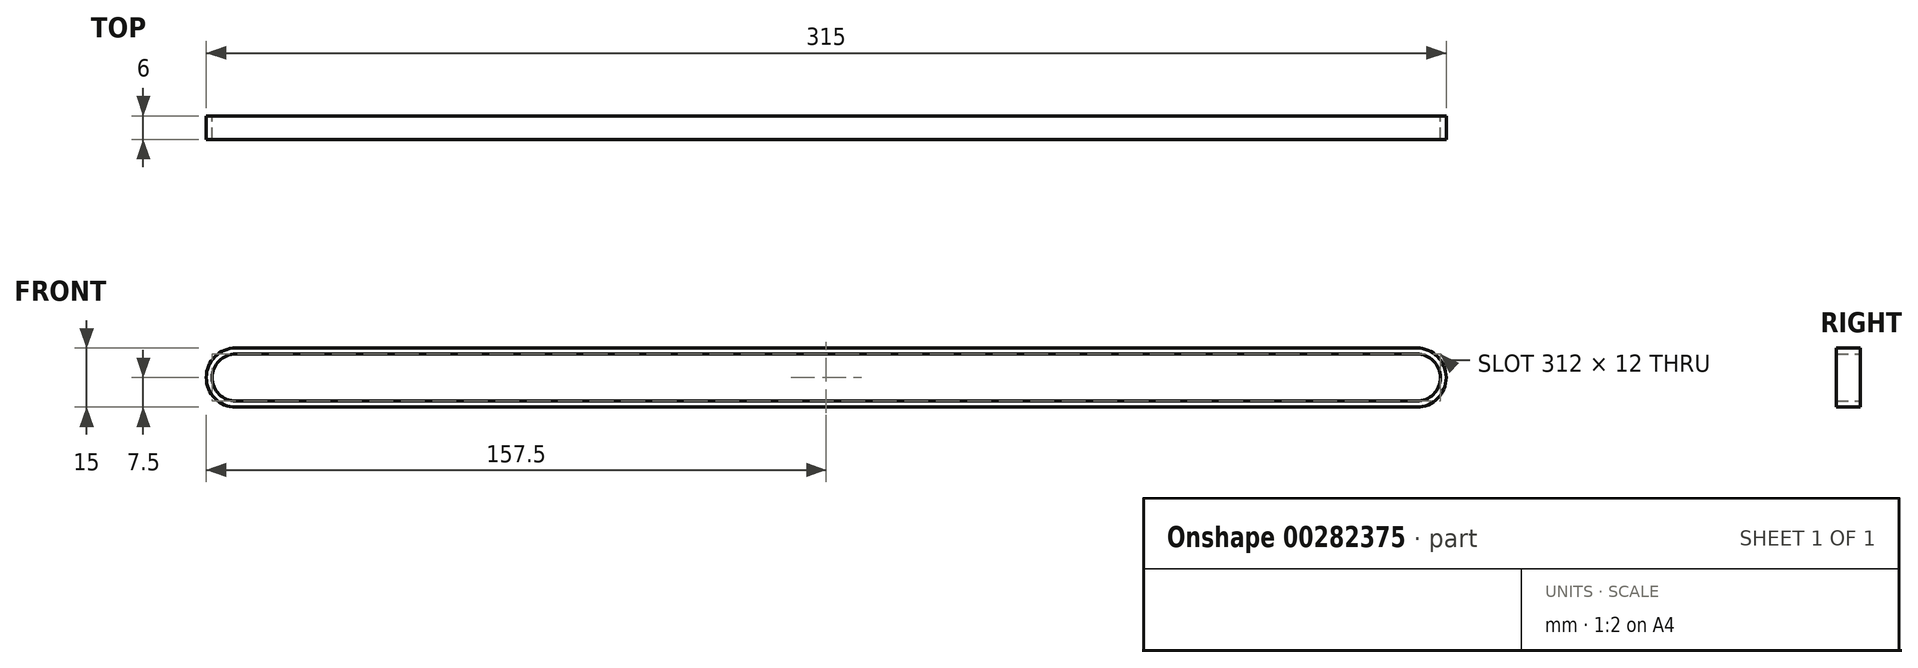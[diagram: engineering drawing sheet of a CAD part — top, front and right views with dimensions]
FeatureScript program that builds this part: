
annotation { "Feature Type Name" : "Feature", "Feature Type Description" : "" }
export const myFeature = defineFeature(function(context is Context, id is Id, definition is map)
    precondition{}
    {
        {
            var Q0;
            Q0=qCreatedBy(makeId("Front.planeOp"),FACE);
            var sketch = newSketch(context, id + "F0", { "sketchPlane" : qUnion([Q0])});
            skArc(sketch, "E0", {"start": v(0, 6) * mm, "mid": v(-6, 0) * mm, "end": v(0, -6) * mm});
            skArc(sketch, "E1", {"start": v(0, 7.5) * mm, "mid": v(-7.5, 0) * mm, "end": v(0, -7.5) * mm});
            skLineSegment(sketch, "E2", {"start": v(0, 0) * mm, "end": v(300, 0) * mm, "construction": true});
            skArc(sketch, "E3", {"start": v(300, -6) * mm, "mid": v(306, 0) * mm, "end": v(300, 6) * mm});
            skArc(sketch, "E4", {"start": v(300, -7.5) * mm, "mid": v(307.5, 0) * mm, "end": v(300, 7.5) * mm});
            skLineSegment(sketch, "E5", {"start": v(0, -7.5) * mm, "end": v(300, -7.5) * mm});
            skLineSegment(sketch, "E6", {"start": v(300, -6) * mm, "end": v(0, -6) * mm});
            skLineSegment(sketch, "E7", {"start": v(0, 6) * mm, "end": v(300, 6) * mm});
            skLineSegment(sketch, "E8", {"start": v(300, 7.5) * mm, "end": v(0, 7.5) * mm});
            skSolve(sketch);
        }
        {
            var Q0;
            Q0=qSketchRegion(id+"F0",true);
            extrude(context, id + "F1", {"entities" : qUnion([Q0]), "depth" : 6 * mm});
        }
    });
